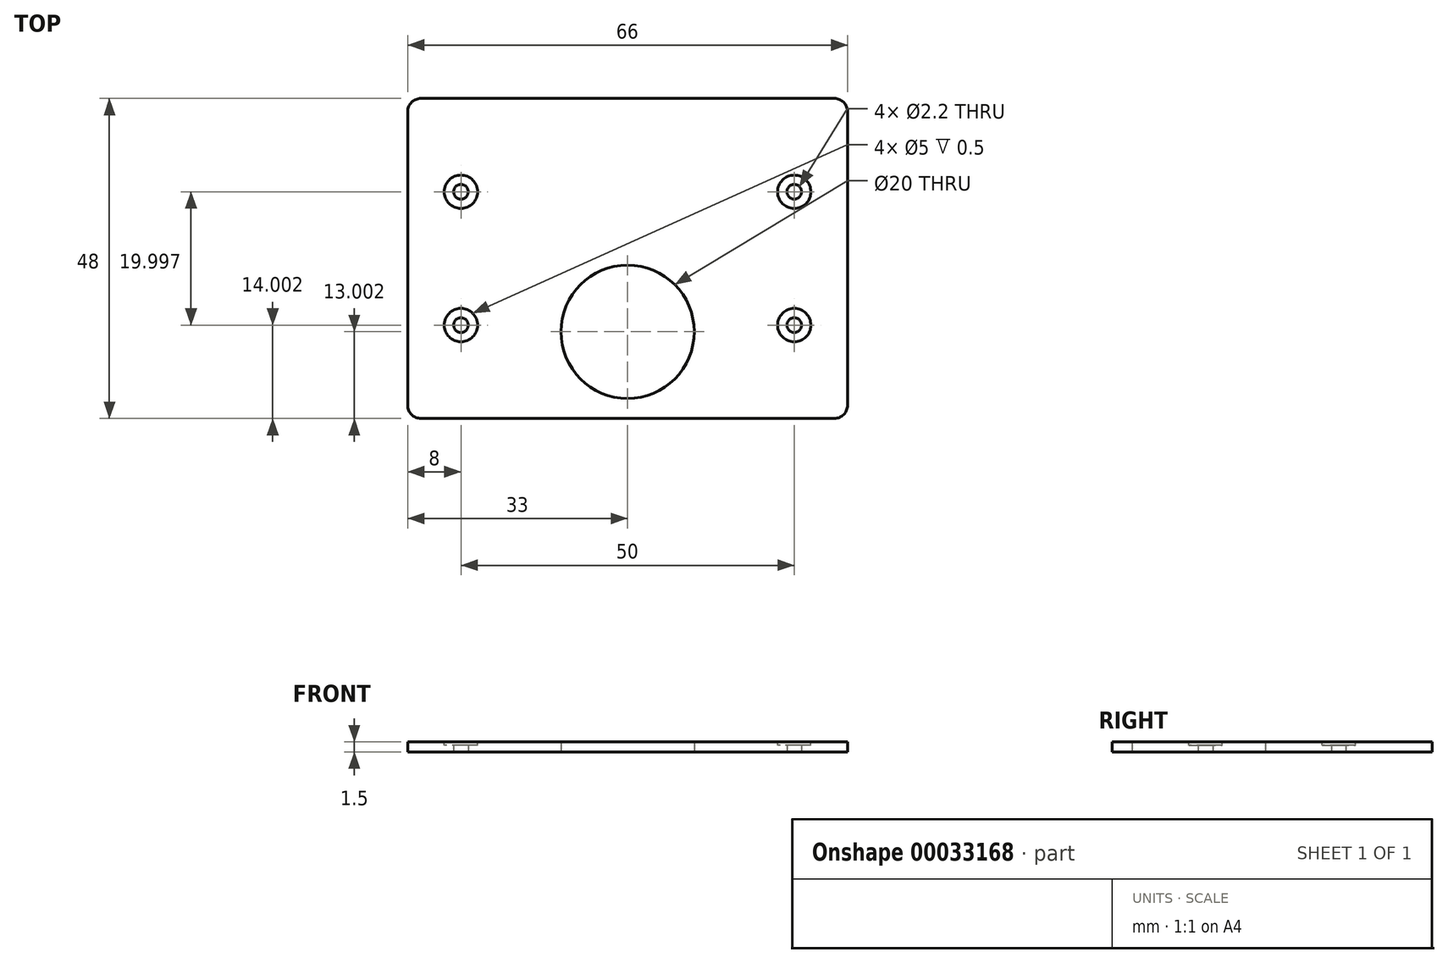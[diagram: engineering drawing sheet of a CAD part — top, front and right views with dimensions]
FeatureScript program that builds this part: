
annotation { "Feature Type Name" : "Feature", "Feature Type Description" : "" }
export const myFeature = defineFeature(function(context is Context, id is Id, definition is map)
    precondition{}
    {
        {
            var Q0;
            Q0=qCreatedBy(makeId("Top.planeOp"),FACE);
            var sketch = newSketch(context, id + "F0", { "sketchPlane" : qUnion([Q0])});
            skLineSegment(sketch, "E0.bottom", {"start": v(-33, 24) * mm, "end": v(33, 24) * mm});
            skLineSegment(sketch, "E0.top", {"start": v(-33, -24) * mm, "end": v(33, -24) * mm});
            skLineSegment(sketch, "E0.left", {"start": v(-33, 24) * mm, "end": v(-33, -24) * mm});
            skLineSegment(sketch, "E0.right", {"start": v(33, 24) * mm, "end": v(33, -24) * mm});
            skPoint(sketch, "E0.middle", {"position": v(0, 0) * mm});
            skCircle(sketch, "E1", {"center": v(-25, 10) * mm, "radius": 1.1 * mm});
            skCircle(sketch, "E2.MirrorC", {"center": v(25, 10) * mm, "radius": 1.1 * mm});
            skCircle(sketch, "E3.MirrorC", {"center": v(-25, -10) * mm, "radius": 1.1 * mm});
            skCircle(sketch, "E4.MirrorC", {"center": v(25, -10) * mm, "radius": 1.1 * mm});
            skCircle(sketch, "E5", {"center": v(0, -11) * mm, "radius": 10 * mm});
            skSolve(sketch);
        }
        {
            var Q0;
            Q0 = qSketchRegion(id + "F0", true);
            extrude(context, id + "F1", {"entities" : qUnion([Q0]), "depth" : 1.5 * mm});
        }
        {
            var Q0;
            Q0=makeQuery(id+"F1.opExtrude","SWEPT_EDGE",EDGE,{"disambiguationData":[OSD([sQuery(id+"F0.wireOp",EDGE,"E0.top"),sQuery(id+"F0.wireOp",EDGE,"E0.left")])]});
            var Q1;
            Q1=makeQuery(id+"F1.opExtrude","SWEPT_EDGE",EDGE,{"disambiguationData":[OSD([sQuery(id+"F0.wireOp",EDGE,"E0.top"),sQuery(id+"F0.wireOp",EDGE,"E0.right")])]});
            var Q2;
            Q2=makeQuery(id+"F1.opExtrude","SWEPT_EDGE",EDGE,{"disambiguationData":[OSD([sQuery(id+"F0.wireOp",EDGE,"E0.bottom"),sQuery(id+"F0.wireOp",EDGE,"E0.left")])]});
            var Q3;
            Q3=makeQuery(id+"F1.opExtrude","SWEPT_EDGE",EDGE,{"disambiguationData":[OSD([sQuery(id+"F0.wireOp",EDGE,"E0.bottom"),sQuery(id+"F0.wireOp",EDGE,"E0.right")])]});
            fillet(context, id + "F2", {"entities" : qUnion([Q0, Q1, Q2, Q3]), "radius" : 2 * mm, "tangentPropagation" : true, "allowEdgeOverflow" : false});
        }
        {
            var Q0;
            Q0=makeQuery(id+"F1.opExtrude","CAP_FACE",FACE,{"disambiguationData":[OSD([sQuery(id+"F0.wireOp",EDGE,"E0.bottom"),sQuery(id+"F0.wireOp",EDGE,"E0.top"),sQuery(id+"F0.wireOp",EDGE,"E0.left"),sQuery(id+"F0.wireOp",EDGE,"E0.right"),sQuery(id+"F0.wireOp",EDGE,"E1"),sQuery(id+"F0.wireOp",EDGE,"E2.MirrorC"),sQuery(id+"F0.wireOp",EDGE,"E3.MirrorC"),sQuery(id+"F0.wireOp",EDGE,"E4.MirrorC"),sQuery(id+"F0.wireOp",EDGE,"E5")])],"isStart":false});
            var sketch = newSketch(context, id + "F3", { "sketchPlane" : qUnion([Q0])});
            skCircle(sketch, "E6", {"center": v(-25, 10) * mm, "radius": 2.5 * mm});
            skCircle(sketch, "E7.MirrorC", {"center": v(25, 10) * mm, "radius": 2.5 * mm});
            skCircle(sketch, "E8.MirrorC", {"center": v(-25, -10) * mm, "radius": 2.5 * mm});
            skCircle(sketch, "E9.MirrorC", {"center": v(25, -10) * mm, "radius": 2.5 * mm});
            skSolve(sketch);
        }
        {
            var Q0;
            Q0 = qSketchRegion(id + "F3", true);
            extrude(context, id + "F4", {"entities" : qUnion([Q0]), "operationType" : NewBodyOperationType.REMOVE, "oppositeDirection" : true, "depth" : 0.5 * mm});
        }
    });
